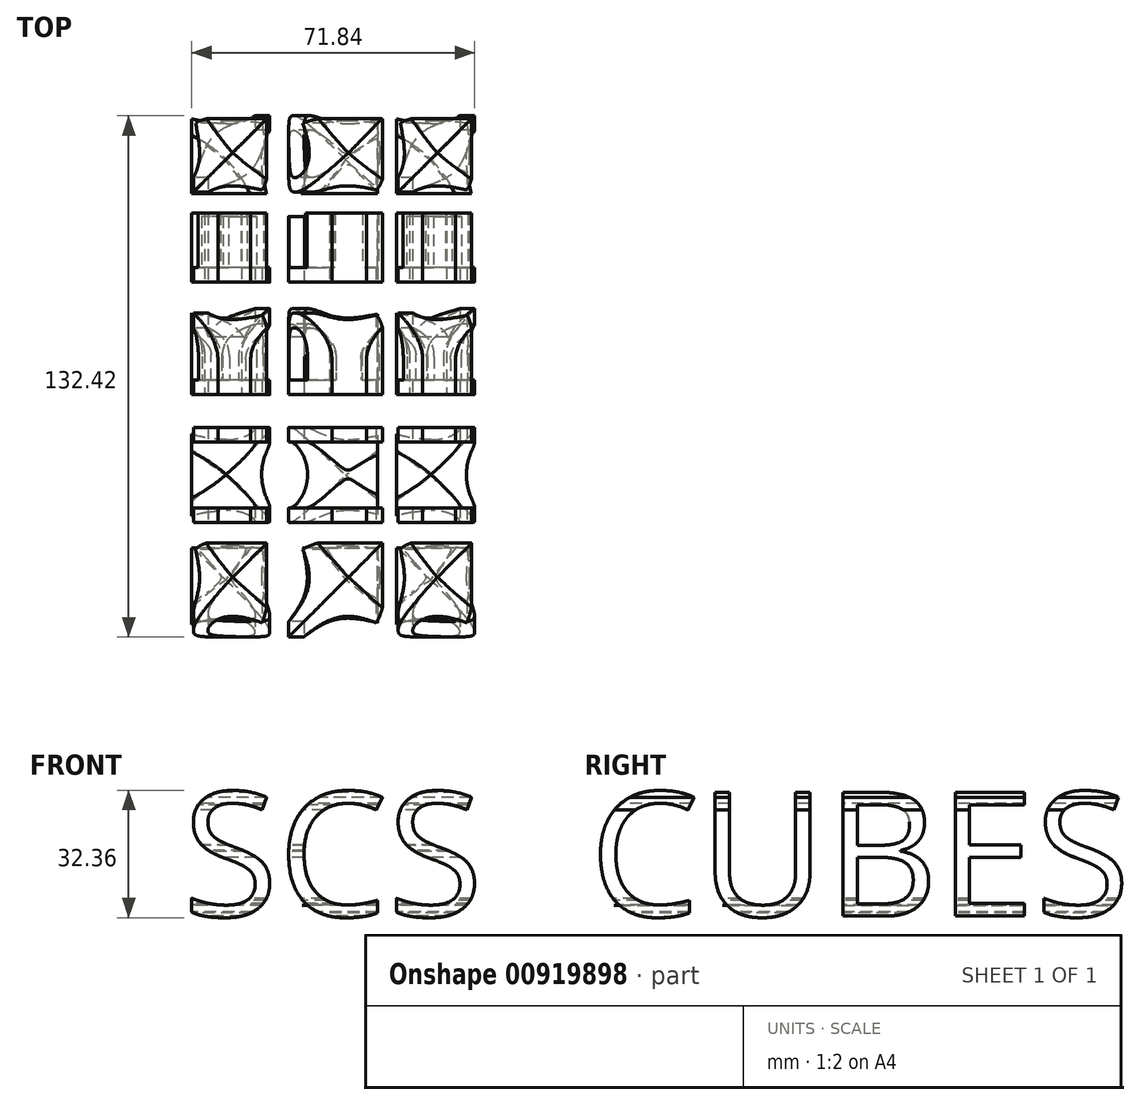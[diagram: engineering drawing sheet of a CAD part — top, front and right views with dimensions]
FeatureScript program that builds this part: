
annotation { "Feature Type Name" : "Feature", "Feature Type Description" : "" }
export const myFeature = defineFeature(function(context is Context, id is Id, definition is map)
    precondition{}
    {
        {
            var Q0;
            Q0=qCreatedBy(makeId("Front.planeOp"),FACE);
            var sketch = newSketch(context, id + "F0", { "sketchPlane" : qUnion([Q0])});
            skText(sketch, "E0", { "text": "SCS", "fontName": "OpenSans-Regular.ttf"});
            const initialGuessF0  = {"E0": [0, -0.03175, 1, 0, 0.03175]};
            skSetInitialGuess(sketch, initialGuessF0);
            skSolve(sketch);
        }
        {
            var Q0;
            Q0=makeQuery(id+"F0.imprint","IMPRINT",FACE,{"disambiguationData":[TD([[makeQuery(id+"F0.imprint","IMPRINT",EDGE,{"derivedFrom":sQuery(id+"F0.wireOp",EDGE,"E0.sketch_text.stroke-0")}),-1.0]])]});
            var Q1;
            Q1 = qSketchRegion(id + "F0", true);
            extrude(context, id + "F1", {"entities" : qUnion([Q0, Q1]), "oppositeDirection" : true, "depth" : 151.7 * mm, "offsetDistance" : 25.4 * mm});
        }
        {
            var Q0;
            Q0=qCreatedBy(makeId("Right.planeOp"),FACE);
            var sketch = newSketch(context, id + "F2", { "sketchPlane" : qUnion([Q0])});
            skText(sketch, "E1", { "text": "CUBES", "fontName": "OpenSans-Regular.ttf"});
            const initialGuessF2  = {"E1": [0, -0.03175, 1, 0, 0.03175]};
            skSetInitialGuess(sketch, initialGuessF2);
            skSolve(sketch);
        }
        {
            var Q0;
            Q0=makeQuery(id+"F2.imprint","IMPRINT",FACE,{"disambiguationData":[TD([[makeQuery(id+"F2.imprint","IMPRINT",EDGE,{"derivedFrom":sQuery(id+"F2.wireOp",EDGE,"E1.sketch_text.stroke-54")}),-1.0]])]});
            var Q1;
            Q1=makeQuery(id+"F2.imprint","IMPRINT",FACE,{"disambiguationData":[TD([[makeQuery(id+"F2.imprint","IMPRINT",EDGE,{"derivedFrom":sQuery(id+"F2.wireOp",EDGE,"E1.sketch_text.stroke-15")}),-1.0]])]});
            var Q2;
            Q2=makeQuery(id+"F2.imprint","IMPRINT",FACE,{"disambiguationData":[TD([[makeQuery(id+"F2.imprint","IMPRINT",EDGE,{"derivedFrom":sQuery(id+"F2.wireOp",EDGE,"E1.sketch_text.stroke-0")}),-1.0]])]});
            var Q3;
            Q3=makeQuery(id+"F2.imprint","IMPRINT",FACE,{"disambiguationData":[TD([[makeQuery(id+"F2.imprint","IMPRINT",EDGE,{"derivedFrom":sQuery(id+"F2.wireOp",EDGE,"E1.sketch_text.stroke-66")}),-1.0]])]});
            var Q4;
            Q4=makeQuery(id+"F2.imprint","IMPRINT",FACE,{"disambiguationData":[TD([[makeQuery(id+"F2.imprint","IMPRINT",EDGE,{"derivedFrom":sQuery(id+"F2.wireOp",EDGE,"E1.sketch_text.stroke-29")}),-1.0]])]});
            extrude(context, id + "F3", {"entities" : qUnion([Q0, Q1, Q2, Q3, Q4]), "operationType" : NewBodyOperationType.INTERSECT, "depth" : 81.1 * mm, "offsetDistance" : 25.4 * mm});
        }
    });
